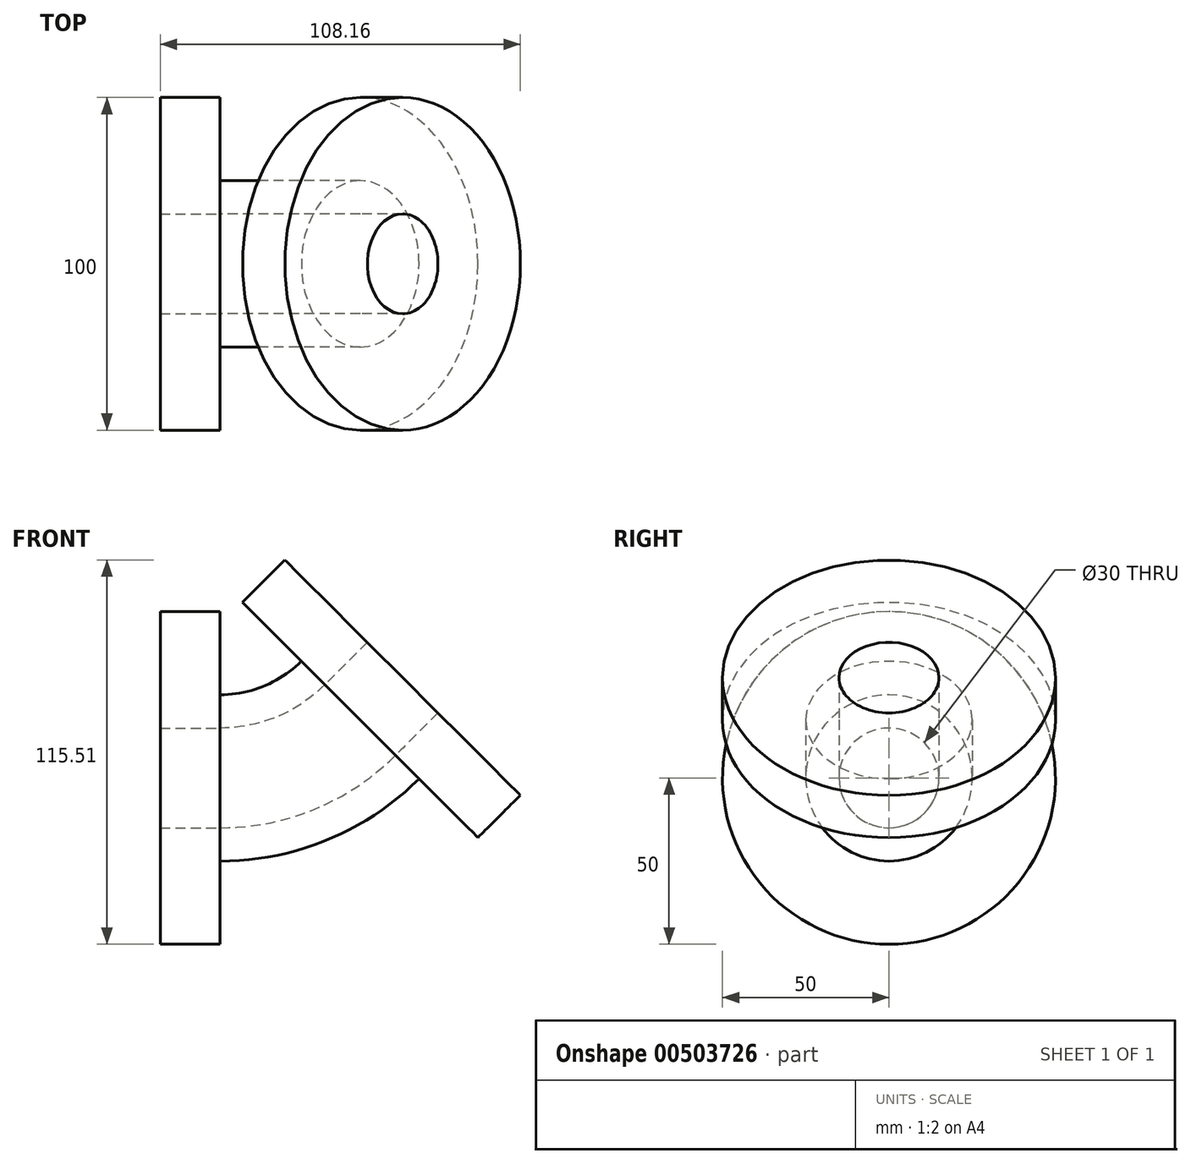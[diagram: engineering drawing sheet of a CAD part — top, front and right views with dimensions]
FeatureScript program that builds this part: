
annotation { "Feature Type Name" : "Feature", "Feature Type Description" : "" }
export const myFeature = defineFeature(function(context is Context, id is Id, definition is map)
    precondition{}
    {
        {
            var Q0;
            Q0=qCreatedBy(makeId("Front.planeOp"),FACE);
            var sketch = newSketch(context, id + "F0", { "sketchPlane" : qUnion([Q0])});
            skLineSegment(sketch, "E0", {"start": v(0, 0) * mm, "end": v(0, -70) * mm, "construction": true});
            skLineSegment(sketch, "E1", {"start": v(0, 0) * mm, "end": v(49.5, -49.5) * mm, "construction": true});
            skArc(sketch, "E2", {"start": v(0, -59.5) * mm, "mid": v(22.77, -54.97) * mm, "end": v(42.07, -42.07) * mm});
            skSolve(sketch);
        }
        {
            var Q0;
            Q0=qCreatedBy(makeId("Right.planeOp"),FACE);
            var sketch = newSketch(context, id + "F1", { "sketchPlane" : qUnion([Q0])});
            skLineSegment(sketch, "E3.0", {"start": v(0, -59.5) * mm, "end": v(0, -42.07) * mm});
            skCircle(sketch, "E4", {"center": v(0, -59.5) * mm, "radius": 50 * mm});
            skCircle(sketch, "E5", {"center": v(0, -59.5) * mm, "radius": 25 * mm});
            skCircle(sketch, "E6", {"center": v(0, -59.5) * mm, "radius": 15 * mm});
            skSolve(sketch);
        }
        {
            var Q0;
            Q0 = qSketchRegion(id + "F1", true);
            var Q1;
            Q1=makeQuery(id+"F1.imprint","IMPRINT",FACE,{"disambiguationData":[TD([[makeQuery(id+"F1.imprint","IMPRINT",EDGE,{"derivedFrom":sQuery(id+"F1.wireOp",EDGE,"E5")}),1.0]])]});
            extrude(context, id + "F2", {"entities" : qUnion([Q0, Q1]), "oppositeDirection" : true, "depth" : 18 * mm});
        }
        {
            var Q0;
            Q0=makeQuery(id+"F1.imprint","IMPRINT",FACE,{"disambiguationData":[TD([[makeQuery(id+"F1.imprint","IMPRINT",EDGE,{"derivedFrom":sQuery(id+"F1.wireOp",EDGE,"E5")}),1.0]])]});
            var Q1;
            Q1=sQuery(id+"F0.wireOp",EDGE,"E2");
            sweep(context, id + "F3", {"operationType" : NewBodyOperationType.ADD, "profiles" : qUnion([Q0]), "path" : qUnion([Q1])});
        }
        {
            var Q0;
            Q0=makeQuery(id+"F3.opSweep","CAP_FACE",FACE,{"disambiguationData":[OSD([sQuery(id+"F0.wireOp",VERTEX,"E2.end"),sQuery(id+"F1.wireOp",EDGE,"E5"),sQuery(id+"F1.wireOp",EDGE,"E6")])],"isStart":false});
            var sketch = newSketch(context, id + "F4", { "sketchPlane" : qUnion([Q0])});
            skCircle(sketch, "E7", {"center": v(0, -59.5) * mm, "radius": 50 * mm});
            skCircle(sketch, "E8", {"center": v(0, -59.5) * mm, "radius": 15 * mm});
            skSolve(sketch);
        }
        {
            var Q0;
            Q0=makeQuery(id+"F4.imprint","IMPRINT",FACE,{"disambiguationData":[TD([[makeQuery(id+"F4.imprint","IMPRINT",EDGE,{"derivedFrom":sQuery(id+"F4.wireOp",EDGE,"E7")}),1.0]])]});
            var Q1;
            Q1=makeQuery(id+"F4.imprint","IMPRINT",FACE,{"disambiguationData":[TD([[makeQuery(id+"F4.imprint","IMPRINT",EDGE,{"derivedFrom":sQuery(id+"F4.wireOp",EDGE,"E8")}),-1.0]])]});
            extrude(context, id + "F5", {"entities" : qUnion([Q0, Q1]), "operationType" : NewBodyOperationType.ADD, "depth" : 18 * mm});
        }
    });
